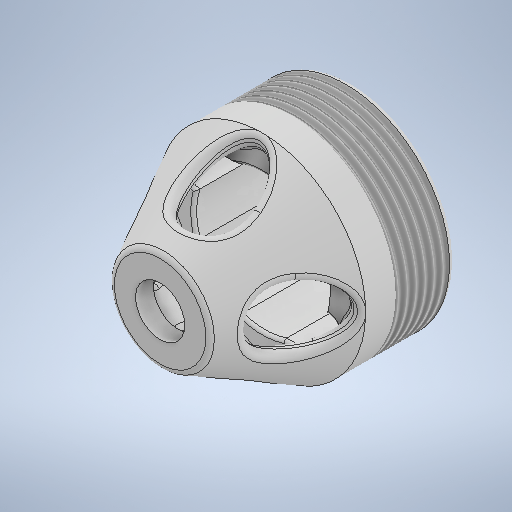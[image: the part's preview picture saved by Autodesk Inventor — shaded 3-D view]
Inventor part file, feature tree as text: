
AUTODESK INVENTOR PART (.ipt)
format: ipt  version: 2025.1 (Build 291241000, 241)  size: 825,344 bytes
history: native  units: mm
features: sketch x7, extrude x5, plane x3, fillet x2, revolve x1, pattern_circular x1, thread x1
ambient origin geometry x8: Origin, YZ Plane, XZ Plane, XY Plane, X Axis, Y Axis, Z Axis, Center Point
bodies: Body1 (feature_tree)
feature tree (20):
  revolve  "Umdrehung1"
  extrude  "Extrusion2"  Depth=2.5mm
  extrude  "Extrusion3"  Depth=30.0mm
  extrude  "Extrusion4"  Depth=8.2mm
  plane  "Arbeitsebene2"
  extrude  "Extrusion5"  Depth=15.0mm TaperAngle=0.0deg
  pattern_circular  "Runde Anordnung1"  [2 undecoded]
  plane  "Arbeitsebene3"
  extrude  "Extrusion6"  Depth=18.0mm TaperAngle=0.0deg
  sketch  "Skizze10"  dims[d20=18.0mm d21=0.0mm d22=22.8mm d23=18.0mm d24=0.0mm d26=0.0mm d27=6.0mm d28=5.0mm d29=7.5mm d30=18.0mm d31=0.0mm d32=40.0mm d33=360.0deg d35=5.5mm d36=5.5mm d37=4.0mm d38=4.0mm d39=18.0mm d40=0.0mm d41=18.0mm d42=14.0mm d43=17.0mm d54=10.0mm d55=0.0mm d56=1.0mm d57=0.5mm d58=34.6mm]
  plane  "Arbeitsebene4"
  thread  "Gewinde2"  [1 undecoded]
  fillet  "Rundung1"  Radius=6.0mm
  fillet  "Rundung2"  Radius=5.0mm
  sketch  "Skizze3"  dims[d4=3.0mm d5=2.5mm d6=2.5mm]
  sketch  "Skizze4"  dims[d8=15.0mm d12=30.0mm]
  sketch  "Skizze5"  dims[d13=14.0mm d14=8.2mm]
  sketch  "Skizze6"  dims[d15=90.0deg d16=15.0mm d17=0.0mm]
  sketch  "Skizze8"  dims[d18=21.6mm]
  sketch  "Skizze9"  dims[d19=21.6mm]
note: 3 required parameter values undecoded (feature->parameter linkage not recoverable at this tier; creation-order binding heuristic only, values carry confidence <= 0.55)
